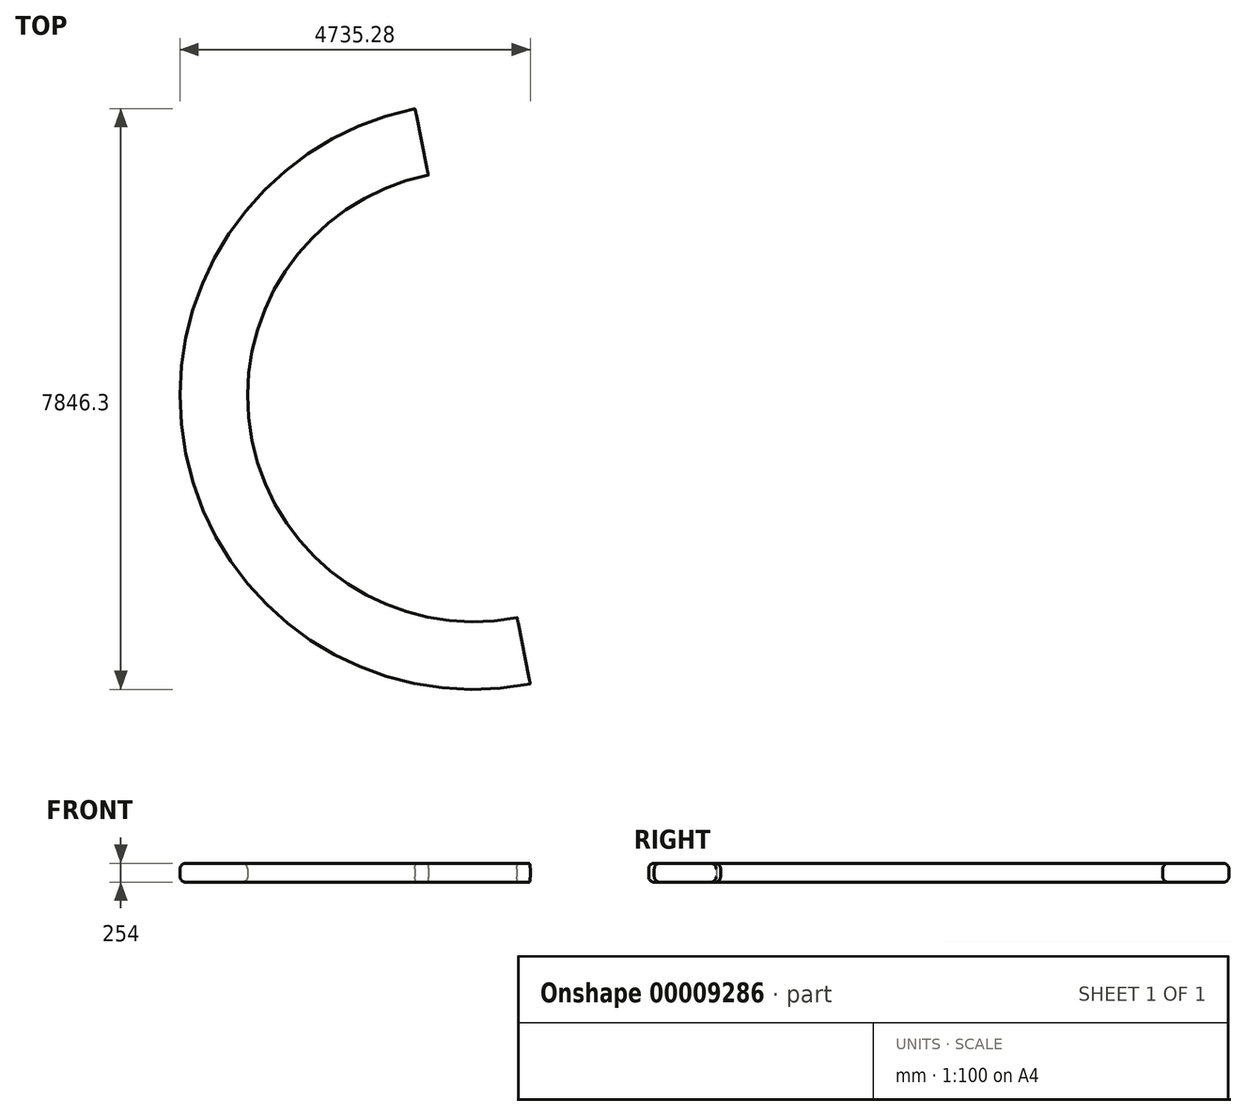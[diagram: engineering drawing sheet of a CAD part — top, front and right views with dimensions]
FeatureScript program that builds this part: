
annotation { "Feature Type Name" : "Feature", "Feature Type Description" : "" }
export const myFeature = defineFeature(function(context is Context, id is Id, definition is map)
    precondition{}
    {
        {
            var Q0;
            Q0=qCreatedBy(makeId("Top.planeOp"),FACE);
            var sketch = newSketch(context, id + "F0", { "sketchPlane" : qUnion([Q0])});
            skArc(sketch, "E0", {"start": v(-605.07, 2987.34) * mm, "mid": v(-2988.54, -599.1) * mm, "end": v(593.15, -2989.73) * mm});
            skArc(sketch, "E1", {"start": v(-784.8, 3883.9) * mm, "mid": v(-3885.1, -778.84) * mm, "end": v(772.88, -3886.3) * mm});
            skLineSegment(sketch, "E2", {"start": v(772.88, -3886.3) * mm, "end": v(593.15, -2989.73) * mm});
            skLineSegment(sketch, "E3.trimOffspring", {"start": v(-605.07, 2987.34) * mm, "end": v(-784.8, 3883.9) * mm});
            skSolve(sketch);
        }
        {
            var Q0;
            Q0=makeQuery(id+"F0.imprint","IMPRINT",FACE,{"disambiguationData":[TD([[makeQuery(id+"F0.imprint","IMPRINT",EDGE,{"derivedFrom":sQuery(id+"F0.wireOp",EDGE,"E0")}),-1.0]])]});
            extrude(context, id + "F1", {"entities" : qUnion([Q0]), "endBound" : BoundingType.SYMMETRIC, "depth" : 254 * mm, "hasSecondDirection" : true, "secondDirectionOppositeDirection" : true, "secondDirectionDepth" : 127 * mm});
        }
        {
            var Q0;
            Q0=makeQuery(id+"F1.opExtrude","CAP_EDGE",EDGE,{"disambiguationData":[OSD([sQuery(id+"F0.wireOp",EDGE,"E1")])],"isStart":false});
            var Q1;
            Q1=makeQuery(id+"F1.opExtrude","CAP_EDGE",EDGE,{"disambiguationData":[OSD([sQuery(id+"F0.wireOp",EDGE,"E0")])],"isStart":false});
            var Q2;
            Q2=makeQuery(id+"F1.opExtrude","CAP_EDGE",EDGE,{"disambiguationData":[OSD([sQuery(id+"F0.wireOp",EDGE,"E0")])],"isStart":true});
            var Q3;
            Q3=makeQuery(id+"F1.opExtrude","CAP_EDGE",EDGE,{"disambiguationData":[OSD([sQuery(id+"F0.wireOp",EDGE,"E1")])],"isStart":true});
            fillet(context, id + "F2", {"entities" : qUnion([Q0, Q1, Q2, Q3]), "radius" : 76.2 * mm, "tangentPropagation" : true, "allowEdgeOverflow" : false});
        }
    });
